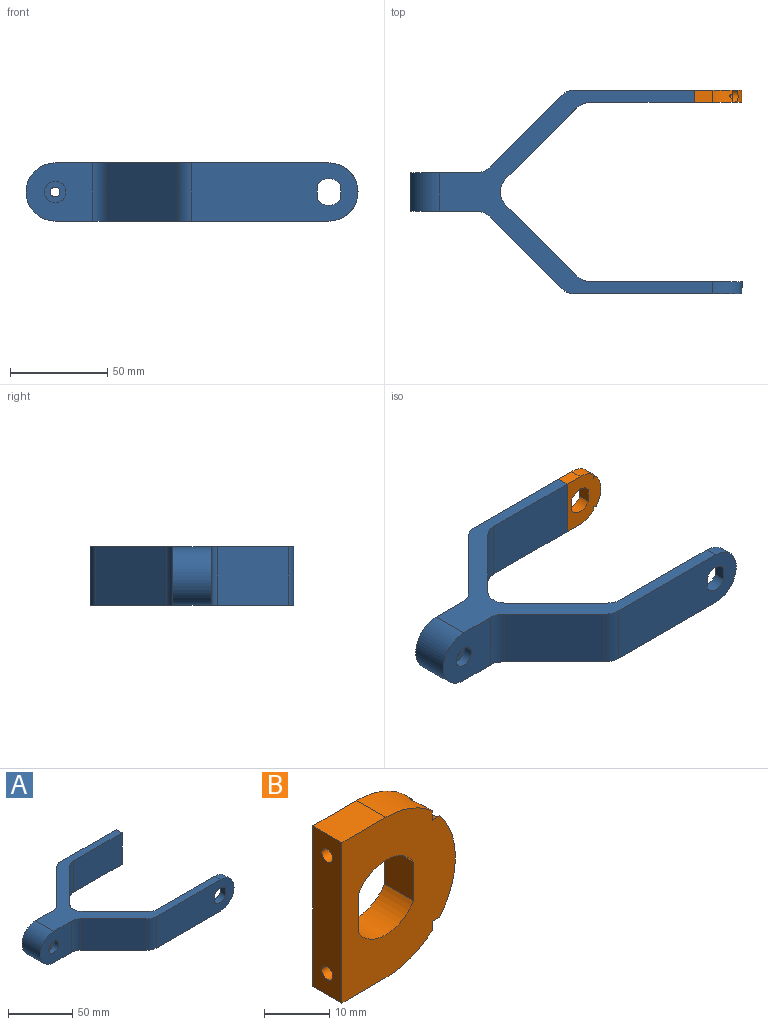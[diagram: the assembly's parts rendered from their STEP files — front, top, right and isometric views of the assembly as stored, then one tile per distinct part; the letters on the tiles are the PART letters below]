
ASSEMBLY  parts=2 mates=1
PART A: 32 faces, bbox 171x105x30 mm
  f0: plane 61.4x30mm, normal (0,1,0), area 1842mm2, adj f11,f12,f29,f31
  f1: cylinder r=2.5mm len=9.86mm, axis (0,-1,0), area 154.9mm2, adj f20,f22
  f2: plane 34.32x30mm, normal (0,1,0), area 837.9mm2, adj f11,f12,f14,f21,f30
  f3: plane 34.32x30mm, normal (0,-1,0), area 837.9mm2, adj f11,f12,f14,f19,f23
  f4: plane 36.64x36.64mm, normal (-0.71,-0.71,0), area 1554.6mm2, adj f11,f12,f23,f24
  f5: plane 85.9x30mm, normal (0,-1,0), area 2336.3mm2, adj f11,f12,f13,f15,f16,f17,f18,f24
  f6: plane 78.06x30mm, normal (0,1,0), area 2101mm2, adj f11,f12,f13,f15,f16,f17,f18,f25
  f7: plane 36.44x36.44mm, normal (0.71,0.71,0), area 1546.1mm2, adj f11,f12,f25,f27
  f8: plane 36.44x36.44mm, normal (0.71,-0.71,0), area 1546.1mm2, adj f11,f12,f26,f28
  f9: plane 53.56x30mm, normal (0,-1,0), area 1606.7mm2, adj f11,f12,f28,f31
  f10: plane 36.64x36.64mm, normal (-0.71,0.71,0), area 1554.6mm2, adj f11,f12,f29,f30
  f11: plane 141x105mm, normal (0,0,1), area 2625.1mm2, adj f0,f2,f3,f4,f5,f6,f7,f8
  f12: plane 141x105mm, normal (0,0,-1), area 2625.1mm2, adj f0,f2,f3,f4,f5,f6,f7,f8
  f13: cylinder r=15mm len=30mm, axis (0,-1,0), area 296.9mm2, adj f5,f6,f11,f12
  f14: cylinder r=15mm len=30mm, axis (0,1,0), area 942.5mm2, adj f2,f3,f11,f12
  f15: plane 7.21x6.3mm, normal (-1,0,0), area 45.4mm2, adj f5,f6,f16,f18
  f16: cylinder r=7mm len=12mm, axis (0,-1,0), area 90.8mm2, adj f5,f6,f15,f17
  f17: plane 7.21x6.3mm, normal (1,0,0), area 45.4mm2, adj f5,f6,f16,f18
  f18: cylinder r=7mm len=12mm, axis (0,-1,0), area 90.8mm2, adj f5,f6,f15,f17
  f19: cylinder r=5.5mm len=11mm, axis (0,-1,0), area 175.2mm2, adj f3,f20
  f20: plane 11x11mm, normal (0,-1,0), area 75.4mm2, adj f1,f19
  f21: cylinder r=5.5mm len=11mm, axis (0,1,0), area 175.2mm2, adj f2,f22
  f22: plane 11x11mm, normal (0,1,0), area 75.4mm2, adj f1,f21
  f23: cylinder r=10mm len=30mm, axis (0,0,1), area 235.6mm2, adj f3,f4,f11,f12
  f24: cylinder r=10mm len=30mm, axis (0,0,-1), area 235.6mm2, adj f4,f5,f11,f12
  f25: cylinder r=10mm len=30mm, axis (0,0,1), area 235.6mm2, adj f6,f7,f11,f12
  f26: cylinder r=10mm len=30mm, axis (0,0,1), area 228.4mm2, adj f8,f11,f12,f27
  f27: cylinder r=10mm len=30mm, axis (0,0,1), area 228.4mm2, adj f7,f11,f12,f26
  f28: cylinder r=10mm len=30mm, axis (0,0,1), area 235.6mm2, adj f8,f9,f11,f12
  f29: cylinder r=10mm len=30mm, axis (0,0,-1), area 235.6mm2, adj f0,f10,f11,f12
  f30: cylinder r=10mm len=30mm, axis (0,0,1), area 235.6mm2, adj f2,f10,f11,f12
  f31: plane 30x6.3mm, normal (1,0,0), area 189mm2, adj f0,f9,f11,f12
PART B: 18 faces, bbox 24.5x6.3x30 mm
  f0: cylinder r=15mm len=10mm, axis (0,1,0), area 66.1mm2, adj f3,f4,f5,f15,f16
  f1: cylinder r=15mm len=18.95mm, axis (0,1,0), area 107.3mm2, adj f3,f4,f14,f17
  f2: cylinder r=15mm len=10mm, axis (0,1,0), area 66.1mm2, adj f3,f4,f7,f12,f13
  f3: plane 30x24.5mm, normal (0,-1,0), area 491.3mm2, adj f0,f1,f2,f5,f6,f7,f8,f9
  f4: plane 30x24.5mm, normal (0,1,0), area 491.3mm2, adj f0,f1,f2,f5,f6,f7,f8,f9
  f5: plane 9.5x6.3mm, normal (0,0,1), area 59.8mm2, adj f0,f3,f4,f6
  f6: plane 30x6.3mm, normal (-1,0,0), area 180mm2, adj f3,f4,f5,f7,f12,f15
  f7: plane 9.5x6.3mm, normal (0,0,-1), area 59.8mm2, adj f2,f3,f4,f6
  f8: cylinder r=7mm len=12mm, axis (0,1,0), area 90.8mm2, adj f3,f4,f9,f11
  f9: plane 7.21x6.3mm, normal (-1,0,0), area 45.4mm2, adj f3,f4,f8,f10
  f10: cylinder r=7mm len=12mm, axis (0,1,0), area 90.8mm2, adj f3,f4,f9,f11
  f11: plane 7.21x6.3mm, normal (1,0,0), area 45.4mm2, adj f3,f4,f8,f10
  f12: cylinder r=1.2mm len=19.5mm, axis (1,0,0), area 144.3mm2, adj f2,f6,f13
  f13: plane 6.3x3.68mm, normal (1,0,0), area 17mm2, adj f2,f3,f4,f12,f14
  f14: cylinder r=3.5mm len=6.3mm, axis (1,0,0), area 20mm2, adj f1,f3,f4,f13
  f15: cylinder r=1.2mm len=19.5mm, axis (1,0,0), area 144.3mm2, adj f0,f6,f16
  f16: plane 6.3x3.68mm, normal (1,0,0), area 17mm2, adj f0,f3,f4,f15,f17
  f17: cylinder r=3.5mm len=6.3mm, axis (1,0,0), area 20mm2, adj f1,f3,f4,f16
PLACE A t=(-89.9,-17.63,14.5)mm fixed
PLACE B t=(10.1,31.72,14.5)mm
MATE fastened A.f31 <-> B.f6  axis (1,0,0) through (10.1,31.72,14.5)mm
